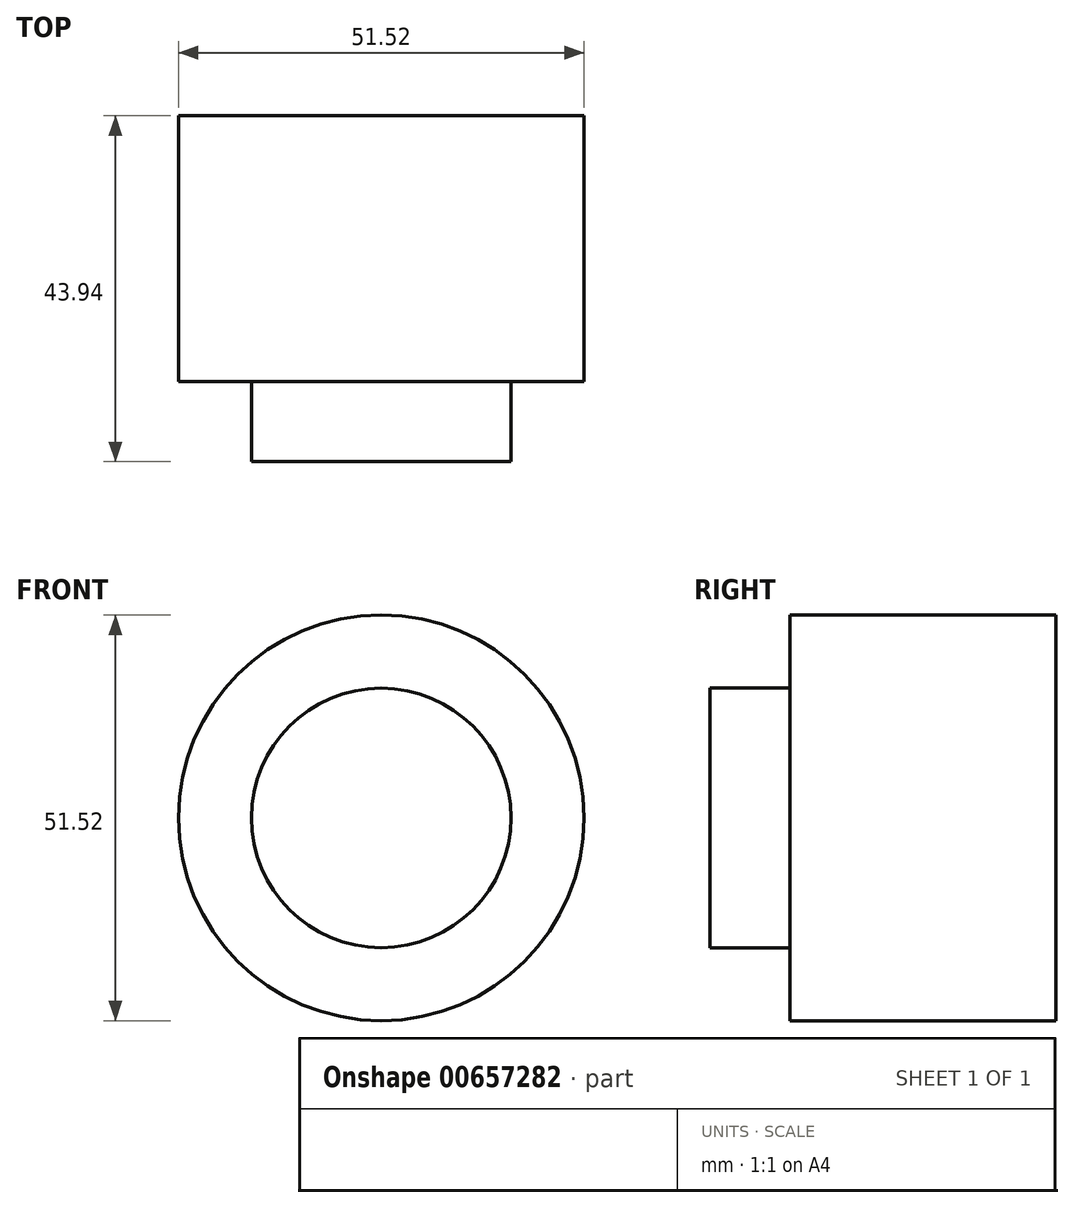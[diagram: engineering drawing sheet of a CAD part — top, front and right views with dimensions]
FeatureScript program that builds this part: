
annotation { "Feature Type Name" : "Feature", "Feature Type Description" : "" }
export const myFeature = defineFeature(function(context is Context, id is Id, definition is map)
    precondition{}
    {
        {
            var Q0;
            Q0=qCreatedBy(makeId("Front.planeOp"),FACE);
            var sketch = newSketch(context, id + "F0", { "sketchPlane" : qUnion([Q0])});
            skCircle(sketch, "E0", {"center": v(0, 0) * mm, "radius": 25.76 * mm});
            skSolve(sketch);
        }
        {
            var Q0;
            Q0 = qSketchRegion(id + "F0", true);
            var Q1;
            Q1=makeQuery(id+"F0.imprint","IMPRINT",FACE,{"disambiguationData":[TD([[makeQuery(id+"F0.imprint","IMPRINT",EDGE,{"derivedFrom":sQuery(id+"F0.wireOp",EDGE,"E0")}),1.0]])]});
            extrude(context, id + "F1", {"entities" : qUnion([Q0, Q1]), "depth" : 33.78 * mm, "offsetDistance" : 25.4 * mm});
        }
        {
            var Q0;
            Q0=makeQuery(id+"F1.opExtrude","CAP_FACE",FACE,{"disambiguationData":[OSD([sQuery(id+"F0.wireOp",EDGE,"E0")])],"isStart":false});
            var sketch = newSketch(context, id + "F2", { "sketchPlane" : qUnion([Q0])});
            skCircle(sketch, "E1", {"center": v(0, 0) * mm, "radius": 16.49 * mm});
            skSolve(sketch);
        }
        {
            var Q0;
            Q0=makeQuery(id+"F2.imprint","IMPRINT",FACE,{"disambiguationData":[TD([[makeQuery(id+"F2.imprint","IMPRINT",EDGE,{"derivedFrom":sQuery(id+"F2.wireOp",EDGE,"E1")}),1.0]])]});
            extrude(context, id + "F3", {"entities" : qUnion([Q0]), "operationType" : NewBodyOperationType.ADD, "depth" : 10.16 * mm, "offsetDistance" : 25.4 * mm});
        }
    });
